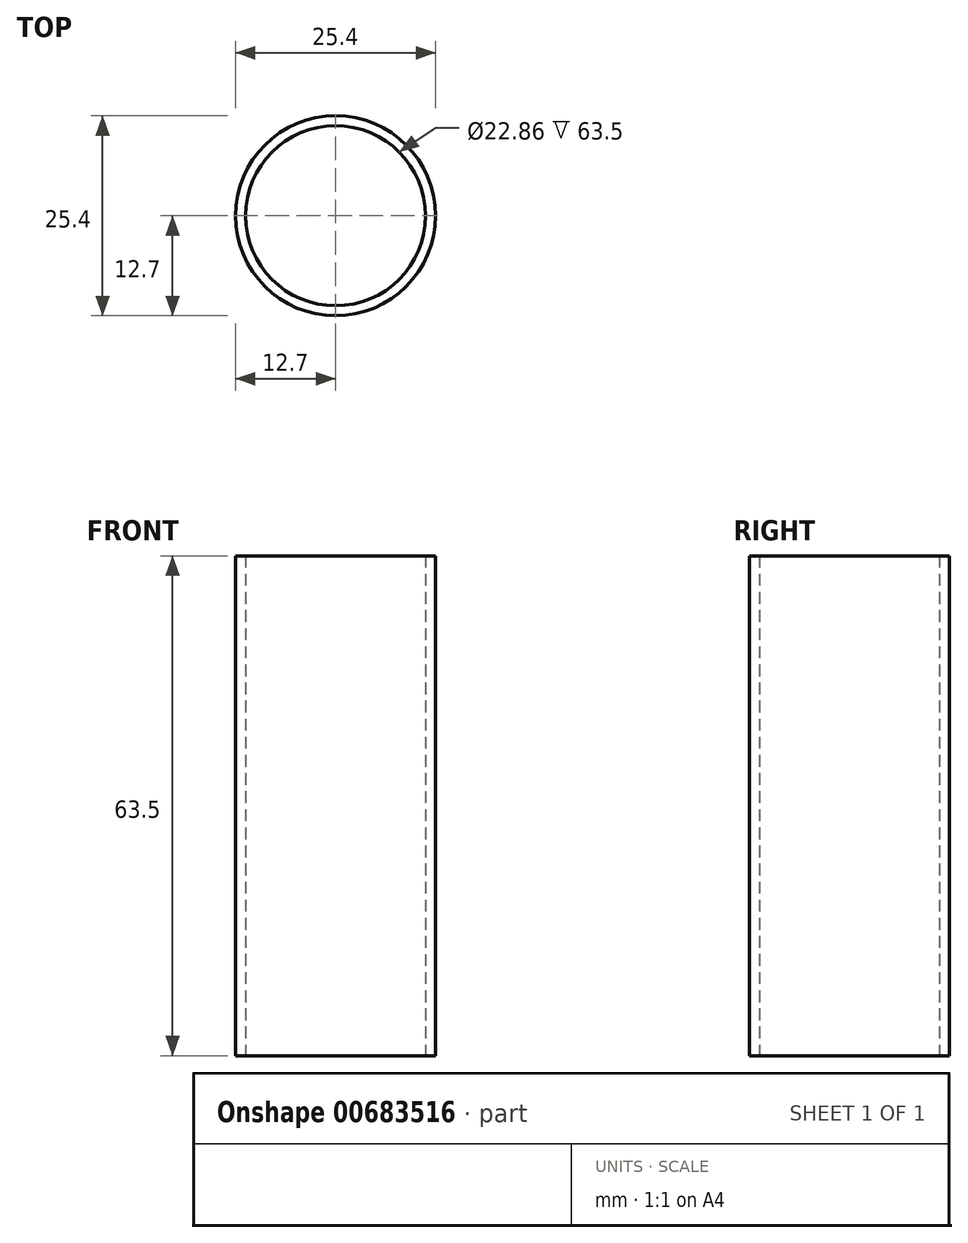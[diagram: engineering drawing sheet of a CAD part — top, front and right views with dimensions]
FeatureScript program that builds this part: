
annotation { "Feature Type Name" : "Feature", "Feature Type Description" : "" }
export const myFeature = defineFeature(function(context is Context, id is Id, definition is map)
    precondition{}
    {
        {
            var Q0;
            Q0=qCreatedBy(makeId("Top.planeOp"),FACE);
            var sketch = newSketch(context, id + "F0", { "sketchPlane" : qUnion([Q0])});
            skCircle(sketch, "E0", {"center": v(0, 0) * mm, "radius": 12.7 * mm});
            skCircle(sketch, "E1", {"center": v(0, 0) * mm, "radius": 11.43 * mm});
            skSolve(sketch);
        }
        {
            var Q0;
            Q0=makeQuery(id+"F0.imprint","IMPRINT",FACE,{"disambiguationData":[TD([[makeQuery(id+"F0.imprint","IMPRINT",EDGE,{"derivedFrom":sQuery(id+"F0.wireOp",EDGE,"E0")}),1.0]])]});
            extrude(context, id + "F1", {"entities" : qUnion([Q0]), "depth" : 63.5 * mm, "offsetDistance" : 25.4 * mm});
        }
    });
